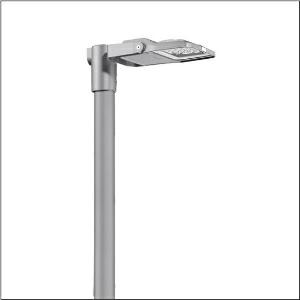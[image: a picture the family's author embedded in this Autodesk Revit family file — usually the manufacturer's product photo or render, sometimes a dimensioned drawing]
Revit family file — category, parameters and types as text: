
# Revit family: floodlight_fl_21_iq_micro___pl43_5xa7761a2a3a_2bb2
name_source: partatom
category: Lighting Fixtures
units: mm (PartAtom-declared; Revit-internal decimal feet)

## family parameters
Cut with Voids When Loaded = No
Host = Face
Light Source = No
Part Type = Normal
Room Calculation Point = No
Round Connector Dimension = Use Diameter
Shared = No

## types (1)
- --- (1 x LED, 3040 lm, 23.1 W, 3000K)
    Apparent Load = 23 VA
    CIE Flux Codes = 29 80 99 100 100
    Color Rendering = 70
    Color Temperature = 3000K
    Default Elevation = 1800 mm
    Description = Floodlight FL 21 iQ micro, floodlight, primary light control with lens, of PMMA, primary optical cover: protective disc, of toughened safety glass, transparent, light distribution: PL43, light emission: direct distribution, installation type: surface-mounted, LED, High Power LED, rated luminous flux: 3.040lm, luminous efficacy: 132lm/W, light colour: 730, colour temperature: 3000K, control: optimised constant luminous flux control (CLO 2.0), Desk-Remote (wireless, voltage-free reading and setting of iQ features in the workshop via application-optimized NFC function/RFID function), Light-Fading, Smart-Wire, Night-Set, Lumen-Switch, Temp-Guard, Auto-Match, with terminal, 6-pole, mains connection: 220..240V, AC, 50/60Hz, start of lifetime: 23W, end of service life: 24W, reduction: 11W, luminaire housing, of diecast aluminium, powder-coated, Siteco® metallic grey (DB 702S), corrosivity category C5 mid according to DIN EN ISO 12944, sealing non-destructively replaceable, please order mast flange separately, mast bracket, of steel, galvanised, powder-coated, Siteco® metallic grey (DB 702S), protection rating (complete): IP66, insulation class (complete): insulation class II (safety insulation), certification: CE, ENEC, VDE, protection symbol: D, impact resistance: IK07, permissible operating ambient temperature: -40..+40°C, permissible operating ambient temperature for outdoor applications: -40..+50°C, standard: DIN EN 12944, LABS conformity tested according to VDMA 24364:2018-05, packaging unit: 1 piece

Light Distribution: PL43
    Height = 65 mm
    Lamp = 1 x LED
    Lamp Light Flux = 3040 lm
    Lamp Power = 23.1 W
    Lamp count = 1
    Length = 312 mm
    Luminous efficacy = 132 lm/W
    Manufacturer = Siteco
    ModVariant = No
    Model = 5XA7761A2A3A
    Number of Poles = 1
    OnlyDefault = Yes
    Power Factor = 1
    Product Name = Floodlight FL 21 iQ micro | PL43
    Product group = floodlight | pylon top
    ProductGroupID = 6101
    Protection Class = Protection class II
    Protection Degree = IP 66
    RLX_Detail_Level = 1
    RLX_Emergency_Light_Flux = 0 lm
    RLX_Emergency_Type = 0
    RLX_Emergency_Type_DB = No
    RlxData = <blob elided: 101773 chars, md5=e4a1f506>
    Socket = socket
    Standby Power = 0 W
    System Light Flux = 3040 lm
    System Power = 23 W
    Type Comments = factory setting: luminous flux: 100 % | dim-lin: 254 | 455 mA
    Type Image = l_1007121.jpg
    URL = http://relux.com
    VarID = @adj_110201
    Voltage = 0 V
    Weight = 0.00 kg
    Width = 230 mm

## geometry (parser evidence)
native form markers: Blend x4, Sweep x13
no freeform markers — native parametric forms only
